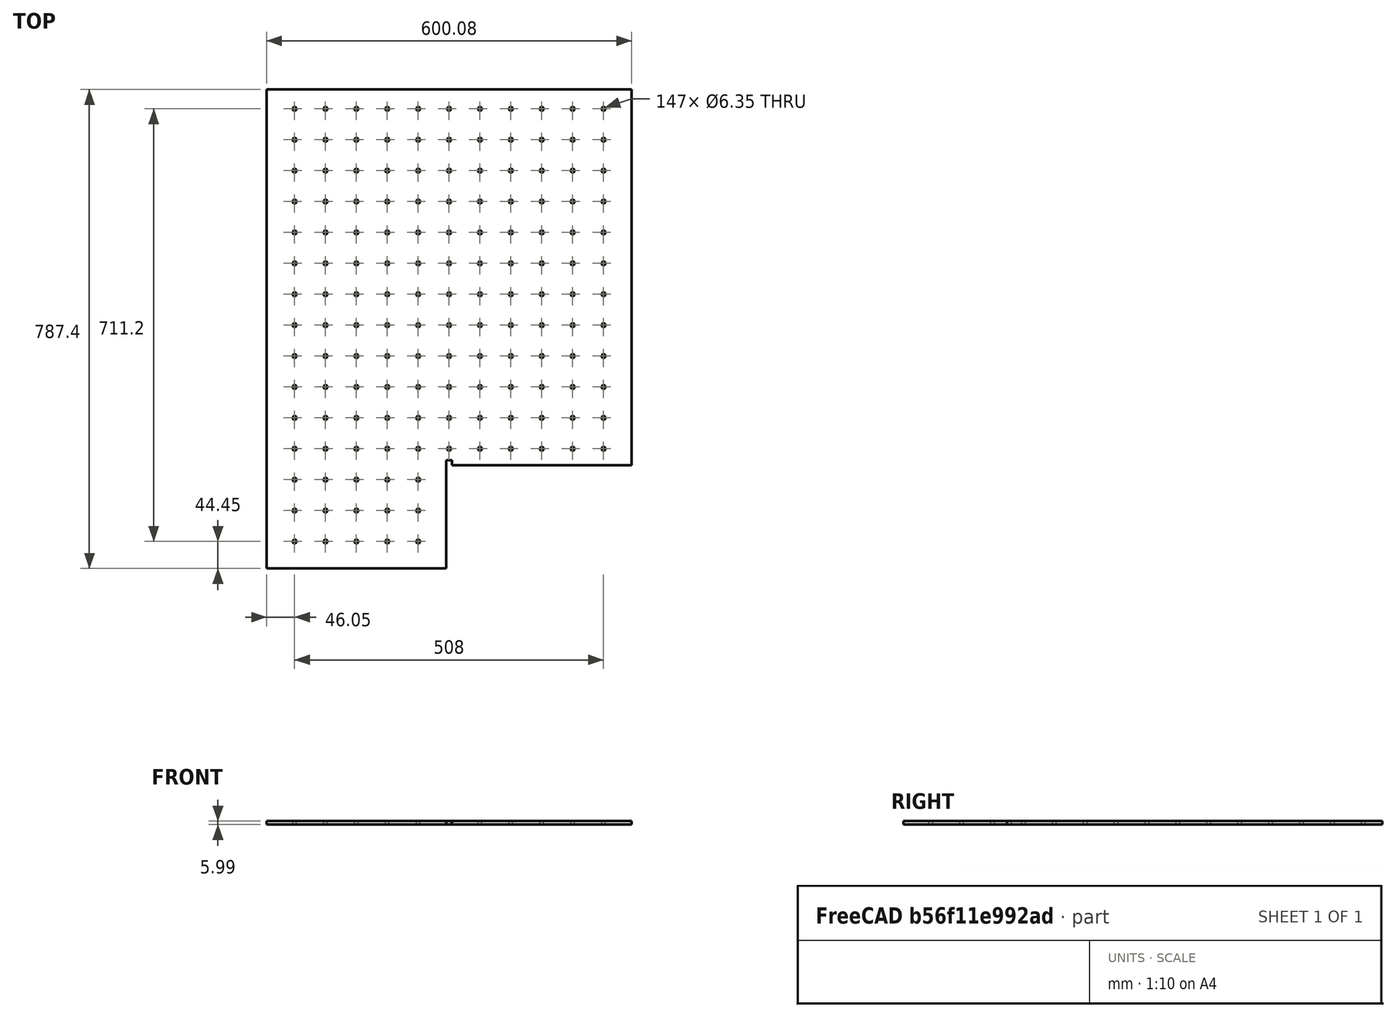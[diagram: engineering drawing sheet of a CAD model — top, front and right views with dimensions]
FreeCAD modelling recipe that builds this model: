
FCSTD DOCUMENT  (FreeCAD 0.19R24267 (Git))
Label: Inv2-P9
License: All rights reserved
LicenseURL: http://en.wikipedia.org/wiki/All_rights_reserved
objects: TechDraw::DrawViewDimension×13, TechDraw::DrawProjGroupItem×2, TechDraw::DrawHatch×2, TechDraw::DrawViewAnnotation×2, Sketcher::SketchObject×1, Part::Extrusion×1, TechDraw::DrawSVGTemplate×1, TechDraw::DrawProjGroup×1, TechDraw::DrawPage×1
note: 2 computed .brp shape members not serialized (recipe doc carries the construction recipe); baked Part::Feature solids carry a one-line shape summary decoded from their .brp

FEATURE [Sketcher::SketchObject] Sketch
  FullyConstrained = false
  sketch-geometry (301):
    g0: LineSegment StartX=0 StartY=0 StartZ=0 EndX=600.075 EndY=0 EndZ=0
    g1: LineSegment StartX=600.075 StartY=0 StartZ=0 EndX=600.075 EndY=-617.55 EndZ=0
    g2: LineSegment StartX=295.275 StartY=-609.6 StartZ=0 EndX=295.275 EndY=-787.4 EndZ=0
    g3: LineSegment StartX=295.275 StartY=-787.4 StartZ=0 EndX=0 EndY=-787.4 EndZ=0
    g4: LineSegment StartX=0 StartY=-787.4 StartZ=0 EndX=0 EndY=0 EndZ=0
    g5: Circle CenterX=46.0502 CenterY=-31.75 CenterZ=0 NormalX=0 NormalY=0 NormalZ=1 AngleXU=0 Radius=3.175
    g6: LineSegment StartX=295.275 StartY=-609.6 StartZ=0 EndX=304.8 EndY=-609.6 EndZ=0
    g7: LineSegment StartX=304.8 StartY=-609.6 StartZ=0 EndX=304.8 EndY=-617.55 EndZ=0
    g8: LineSegment StartX=304.8 StartY=-617.55 StartZ=0 EndX=600.075 EndY=-617.55 EndZ=0
    g9: Circle CenterX=96.8502 CenterY=-31.75 CenterZ=0 NormalX=0 NormalY=0 NormalZ=1 AngleXU=0 Radius=3.175
    g10: LineSegment StartX=46.0502 StartY=-31.75 StartZ=0 EndX=96.8502 EndY=-31.75 EndZ=0
    g11: Circle CenterX=147.65 CenterY=-31.75 CenterZ=0 NormalX=0 NormalY=0 NormalZ=1 AngleXU=0 Radius=3.175
    g12: LineSegment StartX=96.8502 StartY=-31.75 StartZ=0 EndX=147.65 EndY=-31.75 EndZ=0
    g13: Circle CenterX=198.45 CenterY=-31.75 CenterZ=0 NormalX=0 NormalY=0 NormalZ=1 AngleXU=0 Radius=3.175
    g14: LineSegment StartX=147.65 StartY=-31.75 StartZ=0 EndX=198.45 EndY=-31.75 EndZ=0
    g15: Circle CenterX=249.25 CenterY=-31.75 CenterZ=0 NormalX=0 NormalY=0 NormalZ=1 AngleXU=0 Radius=3.175
    g16: LineSegment StartX=198.45 StartY=-31.75 StartZ=0 EndX=249.25 EndY=-31.75 EndZ=0
    g17: Circle CenterX=300.05 CenterY=-31.75 CenterZ=0 NormalX=0 NormalY=0 NormalZ=1 AngleXU=0 Radius=3.175
    g18: LineSegment StartX=249.25 StartY=-31.75 StartZ=0 EndX=300.05 EndY=-31.75 EndZ=0
    g19: Circle CenterX=350.85 CenterY=-31.75 CenterZ=0 NormalX=0 NormalY=0 NormalZ=1 AngleXU=0 Radius=3.175
    g20: LineSegment StartX=300.05 StartY=-31.75 StartZ=0 EndX=350.85 EndY=-31.75 EndZ=0
    g21: Circle CenterX=401.65 CenterY=-31.75 CenterZ=0 NormalX=0 NormalY=0 NormalZ=1 AngleXU=0 Radius=3.175
    g22: LineSegment StartX=350.85 StartY=-31.75 StartZ=0 EndX=401.65 EndY=-31.75 EndZ=0
    g23: Circle CenterX=452.45 CenterY=-31.75 CenterZ=0 NormalX=0 NormalY=0 NormalZ=1 AngleXU=0 Radius=3.175
    g24: LineSegment StartX=401.65 StartY=-31.75 StartZ=0 EndX=452.45 EndY=-31.75 EndZ=0
    g25: Circle CenterX=503.25 CenterY=-31.75 CenterZ=0 NormalX=0 NormalY=0 NormalZ=1 AngleXU=0 Radius=3.175
    g26: LineSegment StartX=452.45 StartY=-31.75 StartZ=0 EndX=503.25 EndY=-31.75 EndZ=0
    g27: Circle CenterX=554.05 CenterY=-31.75 CenterZ=0 NormalX=0 NormalY=0 NormalZ=1 AngleXU=0 Radius=3.175
    g28: LineSegment StartX=503.25 StartY=-31.75 StartZ=0 EndX=554.05 EndY=-31.75 EndZ=0
    g29: Circle CenterX=46.0502 CenterY=-82.55 CenterZ=0 NormalX=0 NormalY=0 NormalZ=1 AngleXU=0 Radius=3.175
    g30: LineSegment StartX=46.0502 StartY=-31.75 StartZ=0 EndX=46.0502 EndY=-82.55 EndZ=0
    g31: Circle CenterX=96.8502 CenterY=-82.55 CenterZ=0 NormalX=0 NormalY=0 NormalZ=1 AngleXU=0 Radius=3.175
    g32: LineSegment StartX=46.0502 StartY=-82.55 StartZ=0 EndX=96.8502 EndY=-82.55 EndZ=0
    g33: Circle CenterX=147.65 CenterY=-82.55 CenterZ=0 NormalX=0 NormalY=0 NormalZ=1 AngleXU=0 Radius=3.175
    g34: LineSegment StartX=96.8502 StartY=-82.55 StartZ=0 EndX=147.65 EndY=-82.55 EndZ=0
    g35: Circle CenterX=198.45 CenterY=-82.55 CenterZ=0 NormalX=0 NormalY=0 NormalZ=1 AngleXU=0 Radius=3.175
    g36: LineSegment StartX=147.65 StartY=-82.55 StartZ=0 EndX=198.45 EndY=-82.55 EndZ=0
    g37: Circle CenterX=249.25 CenterY=-82.55 CenterZ=0 NormalX=0 NormalY=0 NormalZ=1 AngleXU=0 Radius=3.175
    g38: LineSegment StartX=198.45 StartY=-82.55 StartZ=0 EndX=249.25 EndY=-82.55 EndZ=0
    g39: Circle CenterX=300.05 CenterY=-82.55 CenterZ=0 NormalX=0 NormalY=0 NormalZ=1 AngleXU=0 Radius=3.175
    g40: LineSegment StartX=249.25 StartY=-82.55 StartZ=0 EndX=300.05 EndY=-82.55 EndZ=0
    g41: Circle CenterX=350.85 CenterY=-82.55 CenterZ=0 NormalX=0 NormalY=0 NormalZ=1 AngleXU=0 Radius=3.175
    g42: LineSegment StartX=300.05 StartY=-82.55 StartZ=0 EndX=350.85 EndY=-82.55 EndZ=0
    g43: Circle CenterX=401.65 CenterY=-82.55 CenterZ=0 NormalX=0 NormalY=0 NormalZ=1 AngleXU=0 Radius=3.175
    g44: LineSegment StartX=350.85 StartY=-82.55 StartZ=0 EndX=401.65 EndY=-82.55 EndZ=0
    g45: Circle CenterX=452.45 CenterY=-82.55 CenterZ=0 NormalX=0 NormalY=0 NormalZ=1 AngleXU=0 Radius=3.175
    g46: LineSegment StartX=401.65 StartY=-82.55 StartZ=0 EndX=452.45 EndY=-82.55 EndZ=0
    g47: Circle CenterX=503.25 CenterY=-82.55 CenterZ=0 NormalX=0 NormalY=0 NormalZ=1 AngleXU=0 Radius=3.175
    g48: LineSegment StartX=452.45 StartY=-82.55 StartZ=0 EndX=503.25 EndY=-82.55 EndZ=0
    g49: Circle CenterX=554.05 CenterY=-82.55 CenterZ=0 NormalX=0 NormalY=0 NormalZ=1 AngleXU=0 Radius=3.175
    g50: LineSegment StartX=503.25 StartY=-82.55 StartZ=0 EndX=554.05 EndY=-82.55 EndZ=0
    g51: Circle CenterX=46.0502 CenterY=-133.35 CenterZ=0 NormalX=0 NormalY=0 NormalZ=1 AngleXU=0 Radius=3.175
    g52: LineSegment StartX=46.0502 StartY=-82.55 StartZ=0 EndX=46.0502 EndY=-133.35 EndZ=0
    g53: Circle CenterX=96.8502 CenterY=-133.35 CenterZ=0 NormalX=0 NormalY=0 NormalZ=1 AngleXU=0 Radius=3.175
    g54: LineSegment StartX=46.0502 StartY=-133.35 StartZ=0 EndX=96.8502 EndY=-133.35 EndZ=0
    g55: Circle CenterX=147.65 CenterY=-133.35 CenterZ=0 NormalX=0 NormalY=0 NormalZ=1 AngleXU=0 Radius=3.175
    g56: LineSegment StartX=96.8502 StartY=-133.35 StartZ=0 EndX=147.65 EndY=-133.35 EndZ=0
    g57: Circle CenterX=198.45 CenterY=-133.35 CenterZ=0 NormalX=0 NormalY=0 NormalZ=1 AngleXU=0 Radius=3.175
    g58: LineSegment StartX=147.65 StartY=-133.35 StartZ=0 EndX=198.45 EndY=-133.35 EndZ=0
    g59: Circle CenterX=249.25 CenterY=-133.35 CenterZ=0 NormalX=0 NormalY=0 NormalZ=1 AngleXU=0 Radius=3.175
    g60: LineSegment StartX=198.45 StartY=-133.35 StartZ=0 EndX=249.25 EndY=-133.35 EndZ=0
    g61: Circle CenterX=300.05 CenterY=-133.35 CenterZ=0 NormalX=0 NormalY=0 NormalZ=1 AngleXU=0 Radius=3.175
    g62: LineSegment StartX=249.25 StartY=-133.35 StartZ=0 EndX=300.05 EndY=-133.35 EndZ=0
    g63: Circle CenterX=350.85 CenterY=-133.35 CenterZ=0 NormalX=0 NormalY=0 NormalZ=1 AngleXU=0 Radius=3.175
    g64: LineSegment StartX=300.05 StartY=-133.35 StartZ=0 EndX=350.85 EndY=-133.35 EndZ=0
    g65: Circle CenterX=401.65 CenterY=-133.35 CenterZ=0 NormalX=0 NormalY=0 NormalZ=1 AngleXU=0 Radius=3.175
    g66: LineSegment StartX=350.85 StartY=-133.35 StartZ=0 EndX=401.65 EndY=-133.35 EndZ=0
    g67: Circle CenterX=452.45 CenterY=-133.35 CenterZ=0 NormalX=0 NormalY=0 NormalZ=1 AngleXU=0 Radius=3.175
    g68: LineSegment StartX=401.65 StartY=-133.35 StartZ=0 EndX=452.45 EndY=-133.35 EndZ=0
    g69: Circle CenterX=503.25 CenterY=-133.35 CenterZ=0 NormalX=0 NormalY=0 NormalZ=1 AngleXU=0 Radius=3.175
    g70: LineSegment StartX=452.45 StartY=-133.35 StartZ=0 EndX=503.25 EndY=-133.35 EndZ=0
    g71: Circle CenterX=554.05 CenterY=-133.35 CenterZ=0 NormalX=0 NormalY=0 NormalZ=1 AngleXU=0 Radius=3.175
    g72: LineSegment StartX=503.25 StartY=-133.35 StartZ=0 EndX=554.05 EndY=-133.35 EndZ=0
    g73: Circle CenterX=46.0502 CenterY=-184.15 CenterZ=0 NormalX=0 NormalY=0 NormalZ=1 AngleXU=0 Radius=3.175
    g74: LineSegment StartX=46.0502 StartY=-133.35 StartZ=0 EndX=46.0502 EndY=-184.15 EndZ=0
    g75: Circle CenterX=96.8502 CenterY=-184.15 CenterZ=0 NormalX=0 NormalY=0 NormalZ=1 AngleXU=0 Radius=3.175
    g76: LineSegment StartX=46.0502 StartY=-184.15 StartZ=0 EndX=96.8502 EndY=-184.15 EndZ=0
    g77: Circle CenterX=147.65 CenterY=-184.15 CenterZ=0 NormalX=0 NormalY=0 NormalZ=1 AngleXU=0 Radius=3.175
    g78: LineSegment StartX=96.8502 StartY=-184.15 StartZ=0 EndX=147.65 EndY=-184.15 EndZ=0
    g79: Circle CenterX=198.45 CenterY=-184.15 CenterZ=0 NormalX=0 NormalY=0 NormalZ=1 AngleXU=0 Radius=3.175
    g80: LineSegment StartX=147.65 StartY=-184.15 StartZ=0 EndX=198.45 EndY=-184.15 EndZ=0
    g81: Circle CenterX=249.25 CenterY=-184.15 CenterZ=0 NormalX=0 NormalY=0 NormalZ=1 AngleXU=0 Radius=3.175
    g82: LineSegment StartX=198.45 StartY=-184.15 StartZ=0 EndX=249.25 EndY=-184.15 EndZ=0
    g83: Circle CenterX=300.05 CenterY=-184.15 CenterZ=0 NormalX=0 NormalY=0 NormalZ=1 AngleXU=0 Radius=3.175
    g84: LineSegment StartX=249.25 StartY=-184.15 StartZ=0 EndX=300.05 EndY=-184.15 EndZ=0
    g85: Circle CenterX=350.85 CenterY=-184.15 CenterZ=0 NormalX=0 NormalY=0 NormalZ=1 AngleXU=0 Radius=3.175
    g86: LineSegment StartX=300.05 StartY=-184.15 StartZ=0 EndX=350.85 EndY=-184.15 EndZ=0
    g87: Circle CenterX=401.65 CenterY=-184.15 CenterZ=0 NormalX=0 NormalY=0 NormalZ=1 AngleXU=0 Radius=3.175
    g88: LineSegment StartX=350.85 StartY=-184.15 StartZ=0 EndX=401.65 EndY=-184.15 EndZ=0
    g89: Circle CenterX=452.45 CenterY=-184.15 CenterZ=0 NormalX=0 NormalY=0 NormalZ=1 AngleXU=0 Radius=3.175
    g90: LineSegment StartX=401.65 StartY=-184.15 StartZ=0 EndX=452.45 EndY=-184.15 EndZ=0
    g91: Circle CenterX=503.25 CenterY=-184.15 CenterZ=0 NormalX=0 NormalY=0 NormalZ=1 AngleXU=0 Radius=3.175
    g92: LineSegment StartX=452.45 StartY=-184.15 StartZ=0 EndX=503.25 EndY=-184.15 EndZ=0
    g93: Circle CenterX=554.05 CenterY=-184.15 CenterZ=0 NormalX=0 NormalY=0 NormalZ=1 AngleXU=0 Radius=3.175
    g94: LineSegment StartX=503.25 StartY=-184.15 StartZ=0 EndX=554.05 EndY=-184.15 EndZ=0
    g95: Circle CenterX=46.0502 CenterY=-234.95 CenterZ=0 NormalX=0 NormalY=0 NormalZ=1 AngleXU=0 Radius=3.175
    g96: LineSegment StartX=46.0502 StartY=-184.15 StartZ=0 EndX=46.0502 EndY=-234.95 EndZ=0
    g97: Circle CenterX=96.8502 CenterY=-234.95 CenterZ=0 NormalX=0 NormalY=0 NormalZ=1 AngleXU=0 Radius=3.175
    g98: LineSegment StartX=46.0502 StartY=-234.95 StartZ=0 EndX=96.8502 EndY=-234.95 EndZ=0
    g99: Circle CenterX=147.65 CenterY=-234.95 CenterZ=0 NormalX=0 NormalY=0 NormalZ=1 AngleXU=0 Radius=3.175
    g100: LineSegment StartX=96.8502 StartY=-234.95 StartZ=0 EndX=147.65 EndY=-234.95 EndZ=0
    g101: Circle CenterX=198.45 CenterY=-234.95 CenterZ=0 NormalX=0 NormalY=0 NormalZ=1 AngleXU=0 Radius=3.175
    g102: LineSegment StartX=147.65 StartY=-234.95 StartZ=0 EndX=198.45 EndY=-234.95 EndZ=0
    g103: Circle CenterX=249.25 CenterY=-234.95 CenterZ=0 NormalX=0 NormalY=0 NormalZ=1 AngleXU=0 Radius=3.175
    g104: LineSegment StartX=198.45 StartY=-234.95 StartZ=0 EndX=249.25 EndY=-234.95 EndZ=0
    g105: Circle CenterX=300.05 CenterY=-234.95 CenterZ=0 NormalX=0 NormalY=0 NormalZ=1 AngleXU=0 Radius=3.175
    g106: LineSegment StartX=249.25 StartY=-234.95 StartZ=0 EndX=300.05 EndY=-234.95 EndZ=0
    g107: Circle CenterX=350.85 CenterY=-234.95 CenterZ=0 NormalX=0 NormalY=0 NormalZ=1 AngleXU=0 Radius=3.175
    g108: LineSegment StartX=300.05 StartY=-234.95 StartZ=0 EndX=350.85 EndY=-234.95 EndZ=0
    g109: Circle CenterX=401.65 CenterY=-234.95 CenterZ=0 NormalX=0 NormalY=0 NormalZ=1 AngleXU=0 Radius=3.175
    g110: LineSegment StartX=350.85 StartY=-234.95 StartZ=0 EndX=401.65 EndY=-234.95 EndZ=0
    g111: Circle CenterX=452.45 CenterY=-234.95 CenterZ=0 NormalX=0 NormalY=0 NormalZ=1 AngleXU=0 Radius=3.175
    g112: LineSegment StartX=401.65 StartY=-234.95 StartZ=0 EndX=452.45 EndY=-234.95 EndZ=0
    g113: Circle CenterX=503.25 CenterY=-234.95 CenterZ=0 NormalX=0 NormalY=0 NormalZ=1 AngleXU=0 Radius=3.175
    g114: LineSegment StartX=452.45 StartY=-234.95 StartZ=0 EndX=503.25 EndY=-234.95 EndZ=0
    g115: Circle CenterX=554.05 CenterY=-234.95 CenterZ=0 NormalX=0 NormalY=0 NormalZ=1 AngleXU=0 Radius=3.175
    g116: LineSegment StartX=503.25 StartY=-234.95 StartZ=0 EndX=554.05 EndY=-234.95 EndZ=0
    g117: Circle CenterX=46.0502 CenterY=-285.75 CenterZ=0 NormalX=0 NormalY=0 NormalZ=1 AngleXU=0 Radius=3.175
    g118: LineSegment StartX=46.0502 StartY=-234.95 StartZ=0 EndX=46.0502 EndY=-285.75 EndZ=0
    g119: Circle CenterX=96.8502 CenterY=-285.75 CenterZ=0 NormalX=0 NormalY=0 NormalZ=1 AngleXU=0 Radius=3.175
    g120: LineSegment StartX=46.0502 StartY=-285.75 StartZ=0 EndX=96.8502 EndY=-285.75 EndZ=0
    g121: Circle CenterX=147.65 CenterY=-285.75 CenterZ=0 NormalX=0 NormalY=0 NormalZ=1 AngleXU=0 Radius=3.175
    g122: LineSegment StartX=96.8502 StartY=-285.75 StartZ=0 EndX=147.65 EndY=-285.75 EndZ=0
    g123: Circle CenterX=198.45 CenterY=-285.75 CenterZ=0 NormalX=0 NormalY=0 NormalZ=1 AngleXU=0 Radius=3.175
    g124: LineSegment StartX=147.65 StartY=-285.75 StartZ=0 EndX=198.45 EndY=-285.75 EndZ=0
    g125: Circle CenterX=249.25 CenterY=-285.75 CenterZ=0 NormalX=0 NormalY=0 NormalZ=1 AngleXU=0 Radius=3.175
    g126: LineSegment StartX=198.45 StartY=-285.75 StartZ=0 EndX=249.25 EndY=-285.75 EndZ=0
    g127: Circle CenterX=300.05 CenterY=-285.75 CenterZ=0 NormalX=0 NormalY=0 NormalZ=1 AngleXU=0 Radius=3.175
    g128: LineSegment StartX=249.25 StartY=-285.75 StartZ=0 EndX=300.05 EndY=-285.75 EndZ=0
    g129: Circle CenterX=350.85 CenterY=-285.75 CenterZ=0 NormalX=0 NormalY=0 NormalZ=1 AngleXU=0 Radius=3.175
    g130: LineSegment StartX=300.05 StartY=-285.75 StartZ=0 EndX=350.85 EndY=-285.75 EndZ=0
    g131: Circle CenterX=401.65 CenterY=-285.75 CenterZ=0 NormalX=0 NormalY=0 NormalZ=1 AngleXU=0 Radius=3.175
    g132: LineSegment StartX=350.85 StartY=-285.75 StartZ=0 EndX=401.65 EndY=-285.75 EndZ=0
    g133: Circle CenterX=452.45 CenterY=-285.75 CenterZ=0 NormalX=0 NormalY=0 NormalZ=1 AngleXU=0 Radius=3.175
    g134: LineSegment StartX=401.65 StartY=-285.75 StartZ=0 EndX=452.45 EndY=-285.75 EndZ=0
    g135: Circle CenterX=503.25 CenterY=-285.75 CenterZ=0 NormalX=0 NormalY=0 NormalZ=1 AngleXU=0 Radius=3.175
    g136: LineSegment StartX=452.45 StartY=-285.75 StartZ=0 EndX=503.25 EndY=-285.75 EndZ=0
    g137: Circle CenterX=554.05 CenterY=-285.75 CenterZ=0 NormalX=0 NormalY=0 NormalZ=1 AngleXU=0 Radius=3.175
    g138: LineSegment StartX=503.25 StartY=-285.75 StartZ=0 EndX=554.05 EndY=-285.75 EndZ=0
    g139: Circle CenterX=46.0502 CenterY=-336.55 CenterZ=0 NormalX=0 NormalY=0 NormalZ=1 AngleXU=0 Radius=3.175
    g140: LineSegment StartX=46.0502 StartY=-285.75 StartZ=0 EndX=46.0502 EndY=-336.55 EndZ=0
    g141: Circle CenterX=96.8502 CenterY=-336.55 CenterZ=0 NormalX=0 NormalY=0 NormalZ=1 AngleXU=0 Radius=3.175
    g142: LineSegment StartX=46.0502 StartY=-336.55 StartZ=0 EndX=96.8502 EndY=-336.55 EndZ=0
    g143: Circle CenterX=147.65 CenterY=-336.55 CenterZ=0 NormalX=0 NormalY=0 NormalZ=1 AngleXU=0 Radius=3.175
    g144: LineSegment StartX=96.8502 StartY=-336.55 StartZ=0 EndX=147.65 EndY=-336.55 EndZ=0
    g145: Circle CenterX=198.45 CenterY=-336.55 CenterZ=0 NormalX=0 NormalY=0 NormalZ=1 AngleXU=0 Radius=3.175
    g146: LineSegment StartX=147.65 StartY=-336.55 StartZ=0 EndX=198.45 EndY=-336.55 EndZ=0
    g147: Circle CenterX=249.25 CenterY=-336.55 CenterZ=0 NormalX=0 NormalY=0 NormalZ=1 AngleXU=0 Radius=3.175
    g148: LineSegment StartX=198.45 StartY=-336.55 StartZ=0 EndX=249.25 EndY=-336.55 EndZ=0
    g149: Circle CenterX=300.05 CenterY=-336.55 CenterZ=0 NormalX=0 NormalY=0 NormalZ=1 AngleXU=0 Radius=3.175
    g150: LineSegment StartX=249.25 StartY=-336.55 StartZ=0 EndX=300.05 EndY=-336.55 EndZ=0
    g151: Circle CenterX=350.85 CenterY=-336.55 CenterZ=0 NormalX=0 NormalY=0 NormalZ=1 AngleXU=0 Radius=3.175
    g152: LineSegment StartX=300.05 StartY=-336.55 StartZ=0 EndX=350.85 EndY=-336.55 EndZ=0
    g153: Circle CenterX=401.65 CenterY=-336.55 CenterZ=0 NormalX=0 NormalY=0 NormalZ=1 AngleXU=0 Radius=3.175
    g154: LineSegment StartX=350.85 StartY=-336.55 StartZ=0 EndX=401.65 EndY=-336.55 EndZ=0
    g155: Circle CenterX=452.45 CenterY=-336.55 CenterZ=0 NormalX=0 NormalY=0 NormalZ=1 AngleXU=0 Radius=3.175
    g156: LineSegment StartX=401.65 StartY=-336.55 StartZ=0 EndX=452.45 EndY=-336.55 EndZ=0
    g157: Circle CenterX=503.25 CenterY=-336.55 CenterZ=0 NormalX=0 NormalY=0 NormalZ=1 AngleXU=0 Radius=3.175
    g158: LineSegment StartX=452.45 StartY=-336.55 StartZ=0 EndX=503.25 EndY=-336.55 EndZ=0
    g159: Circle CenterX=554.05 CenterY=-336.55 CenterZ=0 NormalX=0 NormalY=0 NormalZ=1 AngleXU=0 Radius=3.175
    g160: LineSegment StartX=503.25 StartY=-336.55 StartZ=0 EndX=554.05 EndY=-336.55 EndZ=0
    g161: Circle CenterX=46.0502 CenterY=-387.35 CenterZ=0 NormalX=0 NormalY=0 NormalZ=1 AngleXU=0 Radius=3.175
    g162: LineSegment StartX=46.0502 StartY=-336.55 StartZ=0 EndX=46.0502 EndY=-387.35 EndZ=0
    g163: Circle CenterX=96.8502 CenterY=-387.35 CenterZ=0 NormalX=0 NormalY=0 NormalZ=1 AngleXU=0 Radius=3.175
    g164: LineSegment StartX=46.0502 StartY=-387.35 StartZ=0 EndX=96.8502 EndY=-387.35 EndZ=0
    g165: Circle CenterX=147.65 CenterY=-387.35 CenterZ=0 NormalX=0 NormalY=0 NormalZ=1 AngleXU=0 Radius=3.175
    g166: LineSegment StartX=96.8502 StartY=-387.35 StartZ=0 EndX=147.65 EndY=-387.35 EndZ=0
    g167: Circle CenterX=198.45 CenterY=-387.35 CenterZ=0 NormalX=0 NormalY=0 NormalZ=1 AngleXU=0 Radius=3.175
    g168: LineSegment StartX=147.65 StartY=-387.35 StartZ=0 EndX=198.45 EndY=-387.35 EndZ=0
    g169: Circle CenterX=249.25 CenterY=-387.35 CenterZ=0 NormalX=0 NormalY=0 NormalZ=1 AngleXU=0 Radius=3.175
    g170: LineSegment StartX=198.45 StartY=-387.35 StartZ=0 EndX=249.25 EndY=-387.35 EndZ=0
    g171: Circle CenterX=300.05 CenterY=-387.35 CenterZ=0 NormalX=0 NormalY=0 NormalZ=1 AngleXU=0 Radius=3.175
    g172: LineSegment StartX=249.25 StartY=-387.35 StartZ=0 EndX=300.05 EndY=-387.35 EndZ=0
    g173: Circle CenterX=350.85 CenterY=-387.35 CenterZ=0 NormalX=0 NormalY=0 NormalZ=1 AngleXU=0 Radius=3.175
    g174: LineSegment StartX=300.05 StartY=-387.35 StartZ=0 EndX=350.85 EndY=-387.35 EndZ=0
    g175: Circle CenterX=401.65 CenterY=-387.35 CenterZ=0 NormalX=0 NormalY=0 NormalZ=1 AngleXU=0 Radius=3.175
    g176: LineSegment StartX=350.85 StartY=-387.35 StartZ=0 EndX=401.65 EndY=-387.35 EndZ=0
    g177: Circle CenterX=452.45 CenterY=-387.35 CenterZ=0 NormalX=0 NormalY=0 NormalZ=1 AngleXU=0 Radius=3.175
    g178: LineSegment StartX=401.65 StartY=-387.35 StartZ=0 EndX=452.45 EndY=-387.35 EndZ=0
    g179: Circle CenterX=503.25 CenterY=-387.35 CenterZ=0 NormalX=0 NormalY=0 NormalZ=1 AngleXU=0 Radius=3.175
    g180: LineSegment StartX=452.45 StartY=-387.35 StartZ=0 EndX=503.25 EndY=-387.35 EndZ=0
    g181: Circle CenterX=554.05 CenterY=-387.35 CenterZ=0 NormalX=0 NormalY=0 NormalZ=1 AngleXU=0 Radius=3.175
    g182: LineSegment StartX=503.25 StartY=-387.35 StartZ=0 EndX=554.05 EndY=-387.35 EndZ=0
    g183: Circle CenterX=46.0502 CenterY=-438.15 CenterZ=0 NormalX=0 NormalY=0 NormalZ=1 AngleXU=0 Radius=3.175
    g184: LineSegment StartX=46.0502 StartY=-387.35 StartZ=0 EndX=46.0502 EndY=-438.15 EndZ=0
    g185: Circle CenterX=96.8502 CenterY=-438.15 CenterZ=0 NormalX=0 NormalY=0 NormalZ=1 AngleXU=0 Radius=3.175
    g186: LineSegment StartX=46.0502 StartY=-438.15 StartZ=0 EndX=96.8502 EndY=-438.15 EndZ=0
    g187: Circle CenterX=147.65 CenterY=-438.15 CenterZ=0 NormalX=0 NormalY=0 NormalZ=1 AngleXU=0 Radius=3.175
    g188: LineSegment StartX=96.8502 StartY=-438.15 StartZ=0 EndX=147.65 EndY=-438.15 EndZ=0
    g189: Circle CenterX=198.45 CenterY=-438.15 CenterZ=0 NormalX=0 NormalY=0 NormalZ=1 AngleXU=0 Radius=3.175
    g190: LineSegment StartX=147.65 StartY=-438.15 StartZ=0 EndX=198.45 EndY=-438.15 EndZ=0
    g191: Circle CenterX=249.25 CenterY=-438.15 CenterZ=0 NormalX=0 NormalY=0 NormalZ=1 AngleXU=0 Radius=3.175
    g192: LineSegment StartX=198.45 StartY=-438.15 StartZ=0 EndX=249.25 EndY=-438.15 EndZ=0
    g193: Circle CenterX=300.05 CenterY=-438.15 CenterZ=0 NormalX=0 NormalY=0 NormalZ=1 AngleXU=0 Radius=3.175
    g194: LineSegment StartX=249.25 StartY=-438.15 StartZ=0 EndX=300.05 EndY=-438.15 EndZ=0
    g195: Circle CenterX=350.85 CenterY=-438.15 CenterZ=0 NormalX=0 NormalY=0 NormalZ=1 AngleXU=0 Radius=3.175
    g196: LineSegment StartX=300.05 StartY=-438.15 StartZ=0 EndX=350.85 EndY=-438.15 EndZ=0
    g197: Circle CenterX=401.65 CenterY=-438.15 CenterZ=0 NormalX=0 NormalY=0 NormalZ=1 AngleXU=0 Radius=3.175
    g198: LineSegment StartX=350.85 StartY=-438.15 StartZ=0 EndX=401.65 EndY=-438.15 EndZ=0
    g199: Circle CenterX=452.45 CenterY=-438.15 CenterZ=0 NormalX=0 NormalY=0 NormalZ=1 AngleXU=0 Radius=3.175
    g200: LineSegment StartX=401.65 StartY=-438.15 StartZ=0 EndX=452.45 EndY=-438.15 EndZ=0
    g201: Circle CenterX=503.25 CenterY=-438.15 CenterZ=0 NormalX=0 NormalY=0 NormalZ=1 AngleXU=0 Radius=3.175
    g202: LineSegment StartX=452.45 StartY=-438.15 StartZ=0 EndX=503.25 EndY=-438.15 EndZ=0
    g203: Circle CenterX=554.05 CenterY=-438.15 CenterZ=0 NormalX=0 NormalY=0 NormalZ=1 AngleXU=0 Radius=3.175
    g204: LineSegment StartX=503.25 StartY=-438.15 StartZ=0 EndX=554.05 EndY=-438.15 EndZ=0
    g205: Circle CenterX=46.0502 CenterY=-488.95 CenterZ=0 NormalX=0 NormalY=0 NormalZ=1 AngleXU=0 Radius=3.175
    g206: LineSegment StartX=46.0502 StartY=-438.15 StartZ=0 EndX=46.0502 EndY=-488.95 EndZ=0
    g207: Circle CenterX=96.8502 CenterY=-488.95 CenterZ=0 NormalX=0 NormalY=0 NormalZ=1 AngleXU=0 Radius=3.175
    g208: LineSegment StartX=46.0502 StartY=-488.95 StartZ=0 EndX=96.8502 EndY=-488.95 EndZ=0
    g209: Circle CenterX=147.65 CenterY=-488.95 CenterZ=0 NormalX=0 NormalY=0 NormalZ=1 AngleXU=0 Radius=3.175
    g210: LineSegment StartX=96.8502 StartY=-488.95 StartZ=0 EndX=147.65 EndY=-488.95 EndZ=0
    g211: Circle CenterX=198.45 CenterY=-488.95 CenterZ=0 NormalX=0 NormalY=0 NormalZ=1 AngleXU=0 Radius=3.175
    g212: LineSegment StartX=147.65 StartY=-488.95 StartZ=0 EndX=198.45 EndY=-488.95 EndZ=0
    g213: Circle CenterX=249.25 CenterY=-488.95 CenterZ=0 NormalX=0 NormalY=0 NormalZ=1 AngleXU=0 Radius=3.175
    g214: LineSegment StartX=198.45 StartY=-488.95 StartZ=0 EndX=249.25 EndY=-488.95 EndZ=0
    g215: Circle CenterX=300.05 CenterY=-488.95 CenterZ=0 NormalX=0 NormalY=0 NormalZ=1 AngleXU=0 Radius=3.175
    g216: LineSegment StartX=249.25 StartY=-488.95 StartZ=0 EndX=300.05 EndY=-488.95 EndZ=0
    g217: Circle CenterX=350.85 CenterY=-488.95 CenterZ=0 NormalX=0 NormalY=0 NormalZ=1 AngleXU=0 Radius=3.175
    g218: LineSegment StartX=300.05 StartY=-488.95 StartZ=0 EndX=350.85 EndY=-488.95 EndZ=0
    g219: Circle CenterX=401.65 CenterY=-488.95 CenterZ=0 NormalX=0 NormalY=0 NormalZ=1 AngleXU=0 Radius=3.175
    g220: LineSegment StartX=350.85 StartY=-488.95 StartZ=0 EndX=401.65 EndY=-488.95 EndZ=0
    g221: Circle CenterX=452.45 CenterY=-488.95 CenterZ=0 NormalX=0 NormalY=0 NormalZ=1 AngleXU=0 Radius=3.175
    g222: LineSegment StartX=401.65 StartY=-488.95 StartZ=0 EndX=452.45 EndY=-488.95 EndZ=0
    g223: Circle CenterX=503.25 CenterY=-488.95 CenterZ=0 NormalX=0 NormalY=0 NormalZ=1 AngleXU=0 Radius=3.175
    g224: LineSegment StartX=452.45 StartY=-488.95 StartZ=0 EndX=503.25 EndY=-488.95 EndZ=0
    g225: Circle CenterX=554.05 CenterY=-488.95 CenterZ=0 NormalX=0 NormalY=0 NormalZ=1 AngleXU=0 Radius=3.175
    g226: LineSegment StartX=503.25 StartY=-488.95 StartZ=0 EndX=554.05 EndY=-488.95 EndZ=0
    g227: Circle CenterX=46.0502 CenterY=-539.75 CenterZ=0 NormalX=0 NormalY=0 NormalZ=1 AngleXU=0 Radius=3.175
    g228: LineSegment StartX=46.0502 StartY=-488.95 StartZ=0 EndX=46.0502 EndY=-539.75 EndZ=0
    g229: Circle CenterX=96.8502 CenterY=-539.75 CenterZ=0 NormalX=0 NormalY=0 NormalZ=1 AngleXU=0 Radius=3.175
    g230: LineSegment StartX=46.0502 StartY=-539.75 StartZ=0 EndX=96.8502 EndY=-539.75 EndZ=0
    g231: Circle CenterX=147.65 CenterY=-539.75 CenterZ=0 NormalX=0 NormalY=0 NormalZ=1 AngleXU=0 Radius=3.175
    g232: LineSegment StartX=96.8502 StartY=-539.75 StartZ=0 EndX=147.65 EndY=-539.75 EndZ=0
    g233: Circle CenterX=198.45 CenterY=-539.75 CenterZ=0 NormalX=0 NormalY=0 NormalZ=1 AngleXU=0 Radius=3.175
    g234: LineSegment StartX=147.65 StartY=-539.75 StartZ=0 EndX=198.45 EndY=-539.75 EndZ=0
    g235: Circle CenterX=249.25 CenterY=-539.75 CenterZ=0 NormalX=0 NormalY=0 NormalZ=1 AngleXU=0 Radius=3.175
    g236: LineSegment StartX=198.45 StartY=-539.75 StartZ=0 EndX=249.25 EndY=-539.75 EndZ=0
    g237: Circle CenterX=300.05 CenterY=-539.75 CenterZ=0 NormalX=0 NormalY=0 NormalZ=1 AngleXU=0 Radius=3.175
    g238: LineSegment StartX=249.25 StartY=-539.75 StartZ=0 EndX=300.05 EndY=-539.75 EndZ=0
    g239: Circle CenterX=350.85 CenterY=-539.75 CenterZ=0 NormalX=0 NormalY=0 NormalZ=1 AngleXU=0 Radius=3.175
    g240: LineSegment StartX=300.05 StartY=-539.75 StartZ=0 EndX=350.85 EndY=-539.75 EndZ=0
    g241: Circle CenterX=401.65 CenterY=-539.75 CenterZ=0 NormalX=0 NormalY=0 NormalZ=1 AngleXU=0 Radius=3.175
    g242: LineSegment StartX=350.85 StartY=-539.75 StartZ=0 EndX=401.65 EndY=-539.75 EndZ=0
    g243: Circle CenterX=452.45 CenterY=-539.75 CenterZ=0 NormalX=0 NormalY=0 NormalZ=1 AngleXU=0 Radius=3.175
    g244: LineSegment StartX=401.65 StartY=-539.75 StartZ=0 EndX=452.45 EndY=-539.75 EndZ=0
    g245: Circle CenterX=503.25 CenterY=-539.75 CenterZ=0 NormalX=0 NormalY=0 NormalZ=1 AngleXU=0 Radius=3.175
    g246: LineSegment StartX=452.45 StartY=-539.75 StartZ=0 EndX=503.25 EndY=-539.75 EndZ=0
    g247: Circle CenterX=554.05 CenterY=-539.75 CenterZ=0 NormalX=0 NormalY=0 NormalZ=1 AngleXU=0 Radius=3.175
    g248: LineSegment StartX=503.25 StartY=-539.75 StartZ=0 EndX=554.05 EndY=-539.75 EndZ=0
    g249: Circle CenterX=46.0502 CenterY=-590.55 CenterZ=0 NormalX=0 NormalY=0 NormalZ=1 AngleXU=0 Radius=3.175
    g250: LineSegment StartX=46.0502 StartY=-539.75 StartZ=0 EndX=46.0502 EndY=-590.55 EndZ=0
    g251: Circle CenterX=96.8502 CenterY=-590.55 CenterZ=0 NormalX=0 NormalY=0 NormalZ=1 AngleXU=0 Radius=3.175
    g252: LineSegment StartX=46.0502 StartY=-590.55 StartZ=0 EndX=96.8502 EndY=-590.55 EndZ=0
    g253: Circle CenterX=147.65 CenterY=-590.55 CenterZ=0 NormalX=0 NormalY=0 NormalZ=1 AngleXU=0 Radius=3.175
    g254: LineSegment StartX=96.8502 StartY=-590.55 StartZ=0 EndX=147.65 EndY=-590.55 EndZ=0
    g255: Circle CenterX=198.45 CenterY=-590.55 CenterZ=0 NormalX=0 NormalY=0 NormalZ=1 AngleXU=0 Radius=3.175
    g256: LineSegment StartX=147.65 StartY=-590.55 StartZ=0 EndX=198.45 EndY=-590.55 EndZ=0
    g257: Circle CenterX=249.25 CenterY=-590.55 CenterZ=0 NormalX=0 NormalY=0 NormalZ=1 AngleXU=0 Radius=3.175
    g258: LineSegment StartX=198.45 StartY=-590.55 StartZ=0 EndX=249.25 EndY=-590.55 EndZ=0
    g259: Circle CenterX=300.05 CenterY=-590.55 CenterZ=0 NormalX=0 NormalY=0 NormalZ=1 AngleXU=0 Radius=3.175
    g260: LineSegment StartX=249.25 StartY=-590.55 StartZ=0 EndX=300.05 EndY=-590.55 EndZ=0
    g261: Circle CenterX=350.85 CenterY=-590.55 CenterZ=0 NormalX=0 NormalY=0 NormalZ=1 AngleXU=0 Radius=3.175
    g262: LineSegment StartX=300.05 StartY=-590.55 StartZ=0 EndX=350.85 EndY=-590.55 EndZ=0
    g263: Circle CenterX=401.65 CenterY=-590.55 CenterZ=0 NormalX=0 NormalY=0 NormalZ=1 AngleXU=0 Radius=3.175
    g264: LineSegment StartX=350.85 StartY=-590.55 StartZ=0 EndX=401.65 EndY=-590.55 EndZ=0
    g265: Circle CenterX=452.45 CenterY=-590.55 CenterZ=0 NormalX=0 NormalY=0 NormalZ=1 AngleXU=0 Radius=3.175
    g266: LineSegment StartX=401.65 StartY=-590.55 StartZ=0 EndX=452.45 EndY=-590.55 EndZ=0
    g267: Circle CenterX=503.25 CenterY=-590.55 CenterZ=0 NormalX=0 NormalY=0 NormalZ=1 AngleXU=0 Radius=3.175
    g268: LineSegment StartX=452.45 StartY=-590.55 StartZ=0 EndX=503.25 EndY=-590.55 EndZ=0
    g269: Circle CenterX=554.05 CenterY=-590.55 CenterZ=0 NormalX=0 NormalY=0 NormalZ=1 AngleXU=0 Radius=3.175
    g270: LineSegment StartX=503.25 StartY=-590.55 StartZ=0 EndX=554.05 EndY=-590.55 EndZ=0
    g271: Circle CenterX=46.0502 CenterY=-641.35 CenterZ=0 NormalX=0 NormalY=0 NormalZ=1 AngleXU=0 Radius=3.175
    g272: LineSegment StartX=46.0502 StartY=-590.55 StartZ=0 EndX=46.0502 EndY=-641.35 EndZ=0
    g273: Circle CenterX=96.8502 CenterY=-641.35 CenterZ=0 NormalX=0 NormalY=0 NormalZ=1 AngleXU=0 Radius=3.175
    g274: LineSegment StartX=46.0502 StartY=-641.35 StartZ=0 EndX=96.8502 EndY=-641.35 EndZ=0
    g275: Circle CenterX=147.65 CenterY=-641.35 CenterZ=0 NormalX=0 NormalY=0 NormalZ=1 AngleXU=0 Radius=3.175
    g276: LineSegment StartX=96.8502 StartY=-641.35 StartZ=0 EndX=147.65 EndY=-641.35 EndZ=0
    g277: Circle CenterX=198.45 CenterY=-641.35 CenterZ=0 NormalX=0 NormalY=0 NormalZ=1 AngleXU=0 Radius=3.175
    g278: LineSegment StartX=147.65 StartY=-641.35 StartZ=0 EndX=198.45 EndY=-641.35 EndZ=0
    g279: Circle CenterX=249.25 CenterY=-641.35 CenterZ=0 NormalX=0 NormalY=0 NormalZ=1 AngleXU=0 Radius=3.175
    g280: LineSegment StartX=198.45 StartY=-641.35 StartZ=0 EndX=249.25 EndY=-641.35 EndZ=0
    g281: Circle CenterX=46.0502 CenterY=-692.15 CenterZ=0 NormalX=0 NormalY=0 NormalZ=1 AngleXU=0 Radius=3.175
    g282: LineSegment StartX=46.0502 StartY=-641.35 StartZ=0 EndX=46.0502 EndY=-692.15 EndZ=0
    g283: Circle CenterX=96.8502 CenterY=-692.15 CenterZ=0 NormalX=0 NormalY=0 NormalZ=1 AngleXU=0 Radius=3.175
    g284: LineSegment StartX=46.0502 StartY=-692.15 StartZ=0 EndX=96.8502 EndY=-692.15 EndZ=0
    g285: Circle CenterX=147.65 CenterY=-692.15 CenterZ=0 NormalX=0 NormalY=0 NormalZ=1 AngleXU=0 Radius=3.175
    g286: LineSegment StartX=96.8502 StartY=-692.15 StartZ=0 EndX=147.65 EndY=-692.15 EndZ=0
    g287: Circle CenterX=198.45 CenterY=-692.15 CenterZ=0 NormalX=0 NormalY=0 NormalZ=1 AngleXU=0 Radius=3.175
    g288: LineSegment StartX=147.65 StartY=-692.15 StartZ=0 EndX=198.45 EndY=-692.15 EndZ=0
    g289: Circle CenterX=249.25 CenterY=-692.15 CenterZ=0 NormalX=0 NormalY=0 NormalZ=1 AngleXU=0 Radius=3.175
    g290: LineSegment StartX=198.45 StartY=-692.15 StartZ=0 EndX=249.25 EndY=-692.15 EndZ=0
    g291: Circle CenterX=46.0502 CenterY=-742.95 CenterZ=0 NormalX=0 NormalY=0 NormalZ=1 AngleXU=0 Radius=3.175
    g292: LineSegment StartX=46.0502 StartY=-692.15 StartZ=0 EndX=46.0502 EndY=-742.95 EndZ=0
    g293: Circle CenterX=96.8502 CenterY=-742.95 CenterZ=0 NormalX=0 NormalY=0 NormalZ=1 AngleXU=0 Radius=3.175
    g294: LineSegment StartX=46.0502 StartY=-742.95 StartZ=0 EndX=96.8502 EndY=-742.95 EndZ=0
    g295: Circle CenterX=147.65 CenterY=-742.95 CenterZ=0 NormalX=0 NormalY=0 NormalZ=1 AngleXU=0 Radius=3.175
    g296: LineSegment StartX=96.8502 StartY=-742.95 StartZ=0 EndX=147.65 EndY=-742.95 EndZ=0
    g297: Circle CenterX=198.45 CenterY=-742.95 CenterZ=0 NormalX=0 NormalY=0 NormalZ=1 AngleXU=0 Radius=3.175
    g298: LineSegment StartX=147.65 StartY=-742.95 StartZ=0 EndX=198.45 EndY=-742.95 EndZ=0
    g299: Circle CenterX=249.25 CenterY=-742.95 CenterZ=0 NormalX=0 NormalY=0 NormalZ=1 AngleXU=0 Radius=3.175
    g300: LineSegment StartX=198.45 StartY=-742.95 StartZ=0 EndX=249.25 EndY=-742.95 EndZ=0
  constraints (755):
    c: Coincident(g0,g-1)
    c: PointOnObject(g0,g-1)
    c: Coincident(g1,g0)
    c: Vertical(g1)
    c: Coincident(g3,g2)
    c: PointOnObject(g3,g-2)
    c: Horizontal(g3)
    c: Coincident(g4,g3)
    c: Coincident(g4,g0)
    c: Distance(g0,g1) = 600.075
    c: Distance(g0,g3) = 787.4
    c: Distance(g3,g2) = 295.275
    c: Diameter(g5) = 6.35
    c: Distance(g5,g0) = 31.75
    c: Distance(g5,g4) = 46.0502
    c: Vertical(g2)
    c: Distance(g2,g3) = 177.8
    c: Coincident(g6,g2)
    c: Horizontal(g6)
    c: Coincident(g7,g6)
    c: Vertical(g7)
    c: Coincident(g8,g7)
    c: Horizontal(g8)
    c: Distance(g7,g6) = 7.9502
    c: Distance(g6,g2) = 9.525
    c: Coincident(g8,g1)
    c: Diameter(g9) = 6.35
    c: Coincident(g5,g10)
    c: Coincident(g9,g10)
    c: Angle(g10) = 0
    c: Diameter(g11) = 6.35
    c: Coincident(g9,g12)
    c: Coincident(g11,g12)
    c: Equal(g10,g12)
    c: Parallel(g12,g10)
    c: Diameter(g13) = 6.35
    c: Coincident(g11,g14)
    c: Coincident(g13,g14)
    c: Equal(g10,g14)
    c: Parallel(g14,g10)
    c: Diameter(g15) = 6.35
    c: Coincident(g13,g16)
    c: Coincident(g15,g16)
    c: Equal(g10,g16)
    c: Parallel(g16,g10)
    c: Diameter(g17) = 6.35
    c: Coincident(g15,g18)
    c: Coincident(g17,g18)
    c: Equal(g10,g18)
    c: Parallel(g18,g10)
    c: Diameter(g19) = 6.35
    c: Coincident(g17,g20)
    c: Coincident(g19,g20)
    c: Equal(g10,g20)
    c: Parallel(g20,g10)
    c: Diameter(g21) = 6.35
    c: Coincident(g19,g22)
    c: Coincident(g21,g22)
    c: Equal(g10,g22)
    c: Parallel(g22,g10)
    c: Diameter(g23) = 6.35
    c: Coincident(g21,g24)
    c: Coincident(g23,g24)
    c: Equal(g10,g24)
    c: Parallel(g24,g10)
    c: Diameter(g25) = 6.35
    c: Coincident(g23,g26)
    c: Coincident(g25,g26)
    c: Equal(g10,g26)
    c: Parallel(g26,g10)
    c: Diameter(g27) = 6.35
    c: Coincident(g25,g28)
    c: Coincident(g27,g28)
    c: Equal(g10,g28)
    c: Parallel(g28,g10)
    c: Diameter(g29) = 6.35
    c: Coincident(g5,g30)
    c: Coincident(g29,g30)
    c: Equal(g30,g10)
    c: Perpendicular(g30,g10)
    c: Diameter(g31) = 6.35
    c: Coincident(g29,g32)
    c: Coincident(g31,g32)
    c: Equal(g10,g32)
    c: Parallel(g32,g10)
    c: Diameter(g33) = 6.35
    c: Coincident(g31,g34)
    c: Coincident(g33,g34)
    c: Equal(g10,g34)
    c: Parallel(g34,g10)
    c: Diameter(g35) = 6.35
    c: Coincident(g33,g36)
    c: Coincident(g35,g36)
    c: Equal(g10,g36)
    c: Parallel(g36,g10)
    c: Diameter(g37) = 6.35
    c: Coincident(g35,g38)
    c: Coincident(g37,g38)
    c: Equal(g10,g38)
    c: Parallel(g38,g10)
    c: Diameter(g39) = 6.35
    c: Coincident(g37,g40)
    c: Coincident(g39,g40)
    c: Equal(g10,g40)
    c: Parallel(g40,g10)
    c: Diameter(g41) = 6.35
    c: Coincident(g39,g42)
    c: Coincident(g41,g42)
    c: Equal(g10,g42)
    c: Parallel(g42,g10)
    c: Diameter(g43) = 6.35
    c: Coincident(g41,g44)
    c: Coincident(g43,g44)
    c: Equal(g10,g44)
    c: Parallel(g44,g10)
    c: Diameter(g45) = 6.35
    c: Coincident(g43,g46)
    c: Coincident(g45,g46)
    c: Equal(g10,g46)
    c: Parallel(g46,g10)
    c: Diameter(g47) = 6.35
    c: Coincident(g45,g48)
    c: Coincident(g47,g48)
    c: Equal(g10,g48)
    c: Parallel(g48,g10)
    c: Diameter(g49) = 6.35
    c: Coincident(g47,g50)
    c: Coincident(g49,g50)
    c: Equal(g10,g50)
    c: Parallel(g50,g10)
    c: Diameter(g51) = 6.35
    c: Coincident(g29,g52)
    c: Coincident(g51,g52)
    c: Equal(g30,g52)
    c: Perpendicular(g52,g10)
    c: Diameter(g53) = 6.35
    c: Coincident(g51,g54)
    c: Coincident(g53,g54)
    c: Equal(g10,g54)
    c: Parallel(g54,g10)
    c: Diameter(g55) = 6.35
    c: Coincident(g53,g56)
    c: Coincident(g55,g56)
    c: Equal(g10,g56)
    c: Parallel(g56,g10)
    c: Diameter(g57) = 6.35
    c: Coincident(g55,g58)
    c: Coincident(g57,g58)
    c: Equal(g10,g58)
    c: Parallel(g58,g10)
    c: Diameter(g59) = 6.35
    c: Coincident(g57,g60)
    c: Coincident(g59,g60)
    c: Equal(g10,g60)
    c: Parallel(g60,g10)
    c: Diameter(g61) = 6.35
    c: Coincident(g59,g62)
    c: Coincident(g61,g62)
    c: Equal(g10,g62)
    c: Parallel(g62,g10)
    c: Diameter(g63) = 6.35
    c: Coincident(g61,g64)
    c: Coincident(g63,g64)
    c: Equal(g10,g64)
    c: Parallel(g64,g10)
    c: Diameter(g65) = 6.35
    c: Coincident(g63,g66)
    c: Coincident(g65,g66)
    c: Equal(g10,g66)
    c: Parallel(g66,g10)
    c: Diameter(g67) = 6.35
    c: Coincident(g65,g68)
    c: Coincident(g67,g68)
    c: Equal(g10,g68)
    c: Parallel(g68,g10)
    c: Diameter(g69) = 6.35
    c: Coincident(g67,g70)
    c: Coincident(g69,g70)
    c: Equal(g10,g70)
    c: Parallel(g70,g10)
    c: Diameter(g71) = 6.35
    c: Coincident(g69,g72)
    c: Coincident(g71,g72)
    c: Equal(g10,g72)
    c: Parallel(g72,g10)
    c: Diameter(g73) = 6.35
    c: Coincident(g51,g74)
    c: Coincident(g73,g74)
    c: Equal(g30,g74)
    c: Perpendicular(g74,g10)
    c: Diameter(g75) = 6.35
    c: Coincident(g73,g76)
    c: Coincident(g75,g76)
    c: Equal(g10,g76)
    c: Parallel(g76,g10)
    c: Diameter(g77) = 6.35
    c: Coincident(g75,g78)
    c: Coincident(g77,g78)
    c: Equal(g10,g78)
    c: Parallel(g78,g10)
    c: Diameter(g79) = 6.35
    c: Coincident(g77,g80)
    c: Coincident(g79,g80)
    c: Equal(g10,g80)
    c: Parallel(g80,g10)
    c: Diameter(g81) = 6.35
    c: Coincident(g79,g82)
    c: Coincident(g81,g82)
    c: Equal(g10,g82)
    c: Parallel(g82,g10)
    c: Diameter(g83) = 6.35
    c: Coincident(g81,g84)
    c: Coincident(g83,g84)
    c: Equal(g10,g84)
    c: Parallel(g84,g10)
    c: Diameter(g85) = 6.35
    c: Coincident(g83,g86)
    c: Coincident(g85,g86)
    c: Equal(g10,g86)
    c: Parallel(g86,g10)
    c: Diameter(g87) = 6.35
    c: Coincident(g85,g88)
    c: Coincident(g87,g88)
    c: Equal(g10,g88)
    c: Parallel(g88,g10)
    c: Diameter(g89) = 6.35
    c: Coincident(g87,g90)
    c: Coincident(g89,g90)
    c: Equal(g10,g90)
    c: Parallel(g90,g10)
    c: Diameter(g91) = 6.35
    c: Coincident(g89,g92)
    c: Coincident(g91,g92)
    c: Equal(g10,g92)
    c: Parallel(g92,g10)
    c: Diameter(g93) = 6.35
    c: Coincident(g91,g94)
    c: Coincident(g93,g94)
    c: Equal(g10,g94)
    c: Parallel(g94,g10)
    c: Diameter(g95) = 6.35
    c: Coincident(g73,g96)
    c: Coincident(g95,g96)
    c: Equal(g30,g96)
    c: Perpendicular(g96,g10)
    c: Diameter(g97) = 6.35
    c: Coincident(g95,g98)
    c: Coincident(g97,g98)
    c: Equal(g10,g98)
    c: Parallel(g98,g10)
    c: Diameter(g99) = 6.35
    c: Coincident(g97,g100)
    c: Coincident(g99,g100)
    c: Equal(g10,g100)
    c: Parallel(g100,g10)
    c: Diameter(g101) = 6.35
    c: Coincident(g99,g102)
    c: Coincident(g101,g102)
    c: Equal(g10,g102)
    c: Parallel(g102,g10)
    c: Diameter(g103) = 6.35
    c: Coincident(g101,g104)
    c: Coincident(g103,g104)
    c: Equal(g10,g104)
    c: Parallel(g104,g10)
    c: Diameter(g105) = 6.35
    c: Coincident(g103,g106)
    c: Coincident(g105,g106)
    c: Equal(g10,g106)
    c: Parallel(g106,g10)
    c: Diameter(g107) = 6.35
    c: Coincident(g105,g108)
    c: Coincident(g107,g108)
    c: Equal(g10,g108)
    c: Parallel(g108,g10)
    c: Diameter(g109) = 6.35
    c: Coincident(g107,g110)
    c: Coincident(g109,g110)
    c: Equal(g10,g110)
    c: Parallel(g110,g10)
    c: Diameter(g111) = 6.35
    c: Coincident(g109,g112)
    c: Coincident(g111,g112)
    c: Equal(g10,g112)
    c: Parallel(g112,g10)
    c: Diameter(g113) = 6.35
    c: Coincident(g111,g114)
    c: Coincident(g113,g114)
    c: Equal(g10,g114)
    c: Parallel(g114,g10)
    c: Diameter(g115) = 6.35
    c: Coincident(g113,g116)
    c: Coincident(g115,g116)
    c: Equal(g10,g116)
    c: Parallel(g116,g10)
    c: Diameter(g117) = 6.35
    c: Coincident(g95,g118)
    c: Coincident(g117,g118)
    c: Equal(g30,g118)
    c: Perpendicular(g118,g10)
    c: Diameter(g119) = 6.35
    c: Coincident(g117,g120)
    c: Coincident(g119,g120)
    c: Equal(g10,g120)
    c: Parallel(g120,g10)
    c: Diameter(g121) = 6.35
    c: Coincident(g119,g122)
    c: Coincident(g121,g122)
    c: Equal(g10,g122)
    c: Parallel(g122,g10)
    c: Diameter(g123) = 6.35
    c: Coincident(g121,g124)
    c: Coincident(g123,g124)
    c: Equal(g10,g124)
    c: Parallel(g124,g10)
    c: Diameter(g125) = 6.35
    c: Coincident(g123,g126)
    c: Coincident(g125,g126)
    c: Equal(g10,g126)
    c: Parallel(g126,g10)
    c: Diameter(g127) = 6.35
    c: Coincident(g125,g128)
    c: Coincident(g127,g128)
    c: Equal(g10,g128)
    c: Parallel(g128,g10)
    c: Diameter(g129) = 6.35
    c: Coincident(g127,g130)
    c: Coincident(g129,g130)
    c: Equal(g10,g130)
    c: Parallel(g130,g10)
    c: Diameter(g131) = 6.35
    c: Coincident(g129,g132)
    c: Coincident(g131,g132)
    c: Equal(g10,g132)
    c: Parallel(g132,g10)
    c: Diameter(g133) = 6.35
    c: Coincident(g131,g134)
    c: Coincident(g133,g134)
    c: Equal(g10,g134)
    c: Parallel(g134,g10)
    c: Diameter(g135) = 6.35
    c: Coincident(g133,g136)
    c: Coincident(g135,g136)
    c: Equal(g10,g136)
    c: Parallel(g136,g10)
    c: Diameter(g137) = 6.35
    c: Coincident(g135,g138)
    c: Coincident(g137,g138)
    c: Equal(g10,g138)
    c: Parallel(g138,g10)
    c: Diameter(g139) = 6.35
    c: Coincident(g117,g140)
    c: Coincident(g139,g140)
    c: Equal(g30,g140)
    c: Perpendicular(g140,g10)
    c: Diameter(g141) = 6.35
    c: Coincident(g139,g142)
    c: Coincident(g141,g142)
    c: Equal(g10,g142)
    c: Parallel(g142,g10)
    c: Diameter(g143) = 6.35
    c: Coincident(g141,g144)
    c: Coincident(g143,g144)
    c: Equal(g10,g144)
    c: Parallel(g144,g10)
    c: Diameter(g145) = 6.35
    c: Coincident(g143,g146)
    c: Coincident(g145,g146)
    c: Equal(g10,g146)
    c: Parallel(g146,g10)
    c: Diameter(g147) = 6.35
    c: Coincident(g145,g148)
    c: Coincident(g147,g148)
    c: Equal(g10,g148)
    c: Parallel(g148,g10)
    c: Diameter(g149) = 6.35
    c: Coincident(g147,g150)
    c: Coincident(g149,g150)
    c: Equal(g10,g150)
    c: Parallel(g150,g10)
    c: Diameter(g151) = 6.35
    c: Coincident(g149,g152)
    c: Coincident(g151,g152)
    c: Equal(g10,g152)
    c: Parallel(g152,g10)
    c: Diameter(g153) = 6.35
    c: Coincident(g151,g154)
    c: Coincident(g153,g154)
    c: Equal(g10,g154)
    c: Parallel(g154,g10)
    c: Diameter(g155) = 6.35
    c: Coincident(g153,g156)
    c: Coincident(g155,g156)
    c: Equal(g10,g156)
    c: Parallel(g156,g10)
    c: Diameter(g157) = 6.35
    c: Coincident(g155,g158)
    c: Coincident(g157,g158)
    c: Equal(g10,g158)
    c: Parallel(g158,g10)
    c: Diameter(g159) = 6.35
    c: Coincident(g157,g160)
    c: Coincident(g159,g160)
    c: Equal(g10,g160)
    c: Parallel(g160,g10)
    c: Diameter(g161) = 6.35
    c: Coincident(g139,g162)
    c: Coincident(g161,g162)
    c: Equal(g30,g162)
    c: Perpendicular(g162,g10)
    c: Diameter(g163) = 6.35
    c: Coincident(g161,g164)
    c: Coincident(g163,g164)
    c: Equal(g10,g164)
    c: Parallel(g164,g10)
    c: Diameter(g165) = 6.35
    c: Coincident(g163,g166)
    c: Coincident(g165,g166)
    c: Equal(g10,g166)
    c: Parallel(g166,g10)
    c: Diameter(g167) = 6.35
    c: Coincident(g165,g168)
    c: Coincident(g167,g168)
    c: Equal(g10,g168)
    c: Parallel(g168,g10)
    c: Diameter(g169) = 6.35
    c: Coincident(g167,g170)
    c: Coincident(g169,g170)
    c: Equal(g10,g170)
    c: Parallel(g170,g10)
    c: Diameter(g171) = 6.35
    c: Coincident(g169,g172)
    c: Coincident(g171,g172)
    c: Equal(g10,g172)
    c: Parallel(g172,g10)
    c: Diameter(g173) = 6.35
    c: Coincident(g171,g174)
    c: Coincident(g173,g174)
    c: Equal(g10,g174)
    c: Parallel(g174,g10)
    c: Diameter(g175) = 6.35
    c: Coincident(g173,g176)
    c: Coincident(g175,g176)
    c: Equal(g10,g176)
    c: Parallel(g176,g10)
    c: Diameter(g177) = 6.35
    c: Coincident(g175,g178)
    c: Coincident(g177,g178)
    c: Equal(g10,g178)
    c: Parallel(g178,g10)
    c: Diameter(g179) = 6.35
    c: Coincident(g177,g180)
    c: Coincident(g179,g180)
    c: Equal(g10,g180)
    c: Parallel(g180,g10)
    c: Diameter(g181) = 6.35
    c: Coincident(g179,g182)
    c: Coincident(g181,g182)
    c: Equal(g10,g182)
    c: Parallel(g182,g10)
    c: Diameter(g183) = 6.35
    c: Coincident(g161,g184)
    c: Coincident(g183,g184)
    c: Equal(g30,g184)
    c: Perpendicular(g184,g10)
    c: Diameter(g185) = 6.35
    c: Coincident(g183,g186)
    c: Coincident(g185,g186)
    c: Equal(g10,g186)
    c: Parallel(g186,g10)
    c: Diameter(g187) = 6.35
    c: Coincident(g185,g188)
    c: Coincident(g187,g188)
    c: Equal(g10,g188)
    c: Parallel(g188,g10)
    c: Diameter(g189) = 6.35
    c: Coincident(g187,g190)
    c: Coincident(g189,g190)
    c: Equal(g10,g190)
    c: Parallel(g190,g10)
    c: Diameter(g191) = 6.35
    c: Coincident(g189,g192)
    c: Coincident(g191,g192)
    c: Equal(g10,g192)
    c: Parallel(g192,g10)
    c: Diameter(g193) = 6.35
    c: Coincident(g191,g194)
    c: Coincident(g193,g194)
    c: Equal(g10,g194)
    c: Parallel(g194,g10)
    c: Diameter(g195) = 6.35
    c: Coincident(g193,g196)
    c: Coincident(g195,g196)
    c: Equal(g10,g196)
    c: Parallel(g196,g10)
    c: Diameter(g197) = 6.35
    c: Coincident(g195,g198)
    c: Coincident(g197,g198)
    c: Equal(g10,g198)
    c: Parallel(g198,g10)
    c: Diameter(g199) = 6.35
    c: Coincident(g197,g200)
    c: Coincident(g199,g200)
    c: Equal(g10,g200)
    c: Parallel(g200,g10)
    c: Diameter(g201) = 6.35
    c: Coincident(g199,g202)
    c: Coincident(g201,g202)
    c: Equal(g10,g202)
    c: Parallel(g202,g10)
    c: Diameter(g203) = 6.35
    c: Coincident(g201,g204)
    c: Coincident(g203,g204)
    c: Equal(g10,g204)
    c: Parallel(g204,g10)
    c: Diameter(g205) = 6.35
    c: Coincident(g183,g206)
    c: Coincident(g205,g206)
    c: Equal(g30,g206)
    c: Perpendicular(g206,g10)
    c: Diameter(g207) = 6.35
    c: Coincident(g205,g208)
    c: Coincident(g207,g208)
    c: Equal(g10,g208)
    c: Parallel(g208,g10)
    c: Diameter(g209) = 6.35
    c: Coincident(g207,g210)
    c: Coincident(g209,g210)
    c: Equal(g10,g210)
    c: Parallel(g210,g10)
    c: Diameter(g211) = 6.35
    c: Coincident(g209,g212)
    c: Coincident(g211,g212)
    c: Equal(g10,g212)
    c: Parallel(g212,g10)
    c: Diameter(g213) = 6.35
    c: Coincident(g211,g214)
    c: Coincident(g213,g214)
    c: Equal(g10,g214)
    c: Parallel(g214,g10)
    c: Diameter(g215) = 6.35
    c: Coincident(g213,g216)
    c: Coincident(g215,g216)
    c: Equal(g10,g216)
    c: Parallel(g216,g10)
    c: Diameter(g217) = 6.35
    c: Coincident(g215,g218)
    c: Coincident(g217,g218)
    c: Equal(g10,g218)
    c: Parallel(g218,g10)
    c: Diameter(g219) = 6.35
    c: Coincident(g217,g220)
    c: Coincident(g219,g220)
    c: Equal(g10,g220)
    c: Parallel(g220,g10)
    c: Diameter(g221) = 6.35
    c: Coincident(g219,g222)
    c: Coincident(g221,g222)
    c: Equal(g10,g222)
    c: Parallel(g222,g10)
    c: Diameter(g223) = 6.35
    c: Coincident(g221,g224)
    c: Coincident(g223,g224)
    c: Equal(g10,g224)
    c: Parallel(g224,g10)
    c: Diameter(g225) = 6.35
    c: Coincident(g223,g226)
    c: Coincident(g225,g226)
    c: Equal(g10,g226)
    c: Parallel(g226,g10)
    c: Diameter(g227) = 6.35
    c: Coincident(g205,g228)
    c: Coincident(g227,g228)
    c: Equal(g30,g228)
    c: Perpendicular(g228,g10)
    c: Diameter(g229) = 6.35
    c: Coincident(g227,g230)
    c: Coincident(g229,g230)
    c: Equal(g10,g230)
    c: Parallel(g230,g10)
    c: Diameter(g231) = 6.35
    c: Coincident(g229,g232)
    c: Coincident(g231,g232)
    c: Equal(g10,g232)
    c: Parallel(g232,g10)
    c: Diameter(g233) = 6.35
    c: Coincident(g231,g234)
    c: Coincident(g233,g234)
    c: Equal(g10,g234)
    c: Parallel(g234,g10)
    c: Diameter(g235) = 6.35
    c: Coincident(g233,g236)
    c: Coincident(g235,g236)
    c: Equal(g10,g236)
    c: Parallel(g236,g10)
    c: Diameter(g237) = 6.35
    c: Coincident(g235,g238)
    c: Coincident(g237,g238)
    c: Equal(g10,g238)
    c: Parallel(g238,g10)
    c: Diameter(g239) = 6.35
    c: Coincident(g237,g240)
    c: Coincident(g239,g240)
    c: Equal(g10,g240)
    c: Parallel(g240,g10)
    c: Diameter(g241) = 6.35
    c: Coincident(g239,g242)
    c: Coincident(g241,g242)
    c: Equal(g10,g242)
    c: Parallel(g242,g10)
    c: Diameter(g243) = 6.35
    c: Coincident(g241,g244)
    c: Coincident(g243,g244)
    c: Equal(g10,g244)
    c: Parallel(g244,g10)
    c: Diameter(g245) = 6.35
    c: Coincident(g243,g246)
    c: Coincident(g245,g246)
    c: Equal(g10,g246)
    c: Parallel(g246,g10)
    c: Diameter(g247) = 6.35
    c: Coincident(g245,g248)
    c: Coincident(g247,g248)
    c: Equal(g10,g248)
    c: Parallel(g248,g10)
    c: Diameter(g249) = 6.35
    c: Coincident(g227,g250)
    c: Coincident(g249,g250)
    c: Equal(g30,g250)
    c: Perpendicular(g250,g10)
    c: Diameter(g251) = 6.35
    c: Coincident(g249,g252)
    c: Coincident(g251,g252)
    c: Equal(g10,g252)
    c: Parallel(g252,g10)
    c: Diameter(g253) = 6.35
    c: Coincident(g251,g254)
    c: Coincident(g253,g254)
    c: Equal(g10,g254)
    c: Parallel(g254,g10)
    c: Diameter(g255) = 6.35
    c: Coincident(g253,g256)
    c: Coincident(g255,g256)
    c: Equal(g10,g256)
    c: Parallel(g256,g10)
    c: Diameter(g257) = 6.35
    c: Coincident(g255,g258)
    c: Coincident(g257,g258)
    c: Equal(g10,g258)
    c: Parallel(g258,g10)
    c: Diameter(g259) = 6.35
    c: Coincident(g257,g260)
    c: Coincident(g259,g260)
    c: Equal(g10,g260)
    c: Parallel(g260,g10)
    c: Diameter(g261) = 6.35
    c: Coincident(g259,g262)
    c: Coincident(g261,g262)
    c: Equal(g10,g262)
    c: Parallel(g262,g10)
    c: Diameter(g263) = 6.35
    c: Coincident(g261,g264)
    c: Coincident(g263,g264)
    c: Equal(g10,g264)
    c: Parallel(g264,g10)
    c: Diameter(g265) = 6.35
    c: Coincident(g263,g266)
    c: Coincident(g265,g266)
    c: Equal(g10,g266)
    c: Parallel(g266,g10)
    c: Diameter(g267) = 6.35
    c: Coincident(g265,g268)
    c: Coincident(g267,g268)
    c: Equal(g10,g268)
    c: Parallel(g268,g10)
    c: Diameter(g269) = 6.35
    c: Coincident(g267,g270)
    c: Coincident(g269,g270)
    c: Equal(g10,g270)
    c: Parallel(g270,g10)
    c: Diameter(g271) = 6.35
    c: Coincident(g249,g272)
    c: Coincident(g271,g272)
    c: Equal(g30,g272)
    c: Perpendicular(g272,g10)
    c: Diameter(g273) = 6.35
    c: Coincident(g271,g274)
    c: Coincident(g273,g274)
    c: Equal(g10,g274)
    c: Parallel(g274,g10)
    c: Diameter(g275) = 6.35
    c: Coincident(g273,g276)
    c: Coincident(g275,g276)
    c: Equal(g10,g276)
    c: Parallel(g276,g10)
    c: Diameter(g277) = 6.35
    c: Coincident(g275,g278)
    c: Coincident(g277,g278)
    c: Equal(g10,g278)
    c: Parallel(g278,g10)
    c: Diameter(g279) = 6.35
    c: Coincident(g277,g280)
    c: Coincident(g279,g280)
    c: Equal(g10,g280)
    c: Parallel(g280,g10)
    c: Diameter(g281) = 6.35
    c: Coincident(g271,g282)
    c: Coincident(g281,g282)
    c: Equal(g30,g282)
    c: Perpendicular(g282,g10)
    c: Diameter(g283) = 6.35
    c: Coincident(g281,g284)
    c: Coincident(g283,g284)
    c: Equal(g10,g284)
    c: Parallel(g284,g10)
    c: Diameter(g285) = 6.35
    c: Coincident(g283,g286)
    c: Coincident(g285,g286)
    c: Equal(g10,g286)
    c: Parallel(g286,g10)
    c: Diameter(g287) = 6.35
    c: Coincident(g285,g288)
    c: Coincident(g287,g288)
    c: Equal(g10,g288)
    c: Parallel(g288,g10)
    c: Diameter(g289) = 6.35
    c: Coincident(g287,g290)
    c: Coincident(g289,g290)
    c: Equal(g10,g290)
    c: Parallel(g290,g10)
    c: Diameter(g291) = 6.35
    c: Coincident(g281,g292)
    c: Coincident(g291,g292)
    c: Equal(g30,g292)
    c: Perpendicular(g292,g10)
    c: Diameter(g293) = 6.35
    c: Coincident(g291,g294)
    c: Coincident(g293,g294)
    c: Equal(g10,g294)
    c: Parallel(g294,g10)
    c: Diameter(g295) = 6.35
    c: Coincident(g293,g296)
    c: Coincident(g295,g296)
    c: Equal(g10,g296)
    c: Parallel(g296,g10)
    c: Diameter(g297) = 6.35
    c: Coincident(g295,g298)
    c: Coincident(g297,g298)
    c: Equal(g10,g298)
    c: Parallel(g298,g10)
    c: Diameter(g299) = 6.35
    c: Coincident(g297,g300)
    c: Coincident(g299,g300)
    c: Equal(g10,g300)
    c: Parallel(g300,g10)
FEATURE [Part::Extrusion] Extrude
  Base = -> Sketch
  Dir = (0,0,1)
  DirMode = 2
  FaceMakerClass = Part::FaceMakerBullseye
  LengthFwd = 5.9944
  LengthRev = 0
  Solid = true
  Symmetric = false
FEATURE [TechDraw::DrawSVGTemplate] Template
  Height = 215.9
  Orientation = 1
  Width = 279.4
FEATURE [TechDraw::DrawProjGroupItem] ProjItem  label="Front"
  CoarseView = false
  Direction = (0,0,1)
  Focus = 100
  HardHidden = false
  IsoCount = 0
  IsoHidden = false
  IsoVisible = false
  LockPosition = true
  Perspective = false
  Rotation = 0
  RotationVector = (-1,0,0)
  Scale = 0.2
  ScaleType = 2
  SeamHidden = false
  SeamVisible = true
  SmoothHidden = false
  SmoothVisible = true
  Source = -> [Extrude]
  Type = 0
  X = 0
  XDirection = (1,-1e-16,0)
  Y = 0
FEATURE [TechDraw::DrawProjGroupItem] ProjItem001  label="Left"
  CoarseView = false
  Direction = (-1,1e-16,1e-16)
  Focus = 100
  HardHidden = false
  IsoCount = 0
  IsoHidden = false
  IsoVisible = false
  LockPosition = false
  Perspective = false
  Rotation = 0
  RotationVector = (1,0,0)
  Scale = 0.2
  ScaleType = 2
  SeamHidden = false
  SeamVisible = true
  SmoothHidden = false
  SmoothVisible = true
  Source = -> [Extrude]
  Type = 1
  X = 80.6565
  XDirection = (1e-16,0,1)
  Y = 0
FEATURE [TechDraw::DrawProjGroup] ProjGroup
  Anchor = -> ProjItem
  AutoDistribute = true
  LockPosition = false
  ProjectionType = 0
  Rotation = 0
  Scale = 0.2
  ScaleType = 2
  Source = -> [Extrude]
  Views = -> [ProjItem,ProjItem001]
  X = 150.88
  Y = 93.9359
  spacingX = 15.0114
  spacingY = 15.0114
FEATURE [TechDraw::DrawHatch] Hatch  label="HatchF0"
  HatchPattern = <path>
  Source = -> ProjItem [Face0]
FEATURE [TechDraw::DrawHatch] Hatch001  label="Hatch001F0"
  HatchPattern = <path>
  Source = -> ProjItem001 [Face0]
FEATURE [TechDraw::DrawViewDimension] Dimension
  Arbitrary = false
  ArbitraryTolerances = false
  EqualTolerance = true
  FormatSpec = %.3f
  FormatSpecOverTolerance = %+.3f
  FormatSpecUnderTolerance = %+.3f
  Inverted = false
  LockPosition = false
  MeasureType = 1
  OverTolerance = 0
  References2D = -> [ProjItem]
  Rotation = 0
  ScaleType = 0
  TheoreticalExact = false
  Type = 1
  UnderTolerance = 0
  X = 3.50259
  Y = 104.504
FEATURE [TechDraw::DrawViewDimension] Dimension001
  Arbitrary = false
  ArbitraryTolerances = false
  EqualTolerance = true
  FormatSpec = %.3f
  FormatSpecOverTolerance = %+.3f
  FormatSpecUnderTolerance = %+.3f
  Inverted = false
  LockPosition = false
  MeasureType = 1
  OverTolerance = 0
  References2D = -> [ProjItem001]
  Rotation = 0
  ScaleType = 0
  TheoreticalExact = false
  Type = 1
  UnderTolerance = 0
  X = 19.1934
  Y = 68.1151
FEATURE [TechDraw::DrawViewDimension] Dimension002
  Arbitrary = false
  ArbitraryTolerances = false
  EqualTolerance = true
  FormatSpec = %.3f
  FormatSpecOverTolerance = %+.3f
  FormatSpecUnderTolerance = %+.3f
  Inverted = false
  LockPosition = false
  MeasureType = 1
  OverTolerance = 0
  References2D = -> [ProjItem]
  Rotation = 0
  ScaleType = 0
  TheoreticalExact = false
  Type = 2
  UnderTolerance = 0
  X = -89.4819
  Y = 0.810546
FEATURE [TechDraw::DrawViewDimension] Dimension003
  Arbitrary = false
  ArbitraryTolerances = false
  EqualTolerance = true
  FormatSpec = ⌀%.3f
  FormatSpecOverTolerance = %+.3f
  FormatSpecUnderTolerance = %+.3f
  Inverted = false
  LockPosition = false
  MeasureType = 1
  OverTolerance = 0
  References2D = -> [ProjItem]
  Rotation = 0
  ScaleType = 0
  TheoreticalExact = false
  Type = 5
  UnderTolerance = 0
  X = -69.1699
  Y = 92.9925
FEATURE [TechDraw::DrawViewDimension] Dimension004
  Arbitrary = false
  ArbitraryTolerances = false
  EqualTolerance = true
  FormatSpec = %.3f
  FormatSpecOverTolerance = %+.3f
  FormatSpecUnderTolerance = %+.3f
  Inverted = false
  LockPosition = false
  MeasureType = 1
  OverTolerance = 0
  References2D = -> [ProjItem]
  Rotation = 0
  ScaleType = 0
  TheoreticalExact = false
  Type = 2
  UnderTolerance = 0
  X = -39.3212
  Y = 93.3367
FEATURE [TechDraw::DrawViewDimension] Dimension005
  Arbitrary = false
  ArbitraryTolerances = false
  EqualTolerance = true
  FormatSpec = %.3f
  FormatSpecOverTolerance = %+.3f
  FormatSpecUnderTolerance = %+.3f
  Inverted = false
  LockPosition = false
  MeasureType = 1
  OverTolerance = 0
  References2D = -> [ProjItem]
  Rotation = 0
  ScaleType = 0
  TheoreticalExact = false
  Type = 1
  UnderTolerance = 0
  X = -75.0723
  Y = 62.6699
FEATURE [TechDraw::DrawViewDimension] Dimension006
  Arbitrary = false
  ArbitraryTolerances = false
  EqualTolerance = true
  FormatSpec = %.3f
  FormatSpecOverTolerance = %+.3f
  FormatSpecUnderTolerance = %+.3f
  Inverted = false
  LockPosition = false
  MeasureType = 1
  OverTolerance = 0
  References2D = -> [ProjItem]
  Rotation = 0
  ScaleType = 0
  TheoreticalExact = false
  Type = 2
  UnderTolerance = 0
  X = -28.0142
  Y = 93.0347
FEATURE [TechDraw::DrawViewDimension] Dimension007
  Arbitrary = false
  ArbitraryTolerances = false
  EqualTolerance = true
  FormatSpec = %.3f
  FormatSpecOverTolerance = %+.3f
  FormatSpecUnderTolerance = %+.3f
  Inverted = false
  LockPosition = false
  MeasureType = 1
  OverTolerance = 0
  References2D = -> [ProjItem]
  Rotation = 0
  ScaleType = 0
  TheoreticalExact = false
  Type = 1
  UnderTolerance = 0
  X = -75.1463
  Y = 50.6688
FEATURE [TechDraw::DrawViewDimension] Dimension008
  Arbitrary = false
  ArbitraryTolerances = false
  EqualTolerance = true
  FormatSpec = %.3f
  FormatSpecOverTolerance = %+.3f
  FormatSpecUnderTolerance = %+.3f
  Inverted = false
  LockPosition = false
  MeasureType = 1
  OverTolerance = 0
  References2D = -> [ProjItem]
  Rotation = 0
  ScaleType = 0
  TheoreticalExact = false
  Type = 1
  UnderTolerance = 0
  X = -28.1257
  Y = -19.5461
FEATURE [TechDraw::DrawViewDimension] Dimension009
  Arbitrary = false
  ArbitraryTolerances = false
  EqualTolerance = true
  FormatSpec = %.3f
  FormatSpecOverTolerance = %+.3f
  FormatSpecUnderTolerance = %+.3f
  Inverted = false
  LockPosition = false
  MeasureType = 1
  OverTolerance = 0
  References2D = -> [ProjItem]
  Rotation = 0
  ScaleType = 0
  TheoreticalExact = false
  Type = 1
  UnderTolerance = 0
  X = 29.8638
  Y = -19.4889
FEATURE [TechDraw::DrawViewDimension] Dimension010
  Arbitrary = false
  ArbitraryTolerances = false
  EqualTolerance = true
  FormatSpec = %.3f
  FormatSpecOverTolerance = %+.3f
  FormatSpecUnderTolerance = %+.3f
  Inverted = false
  LockPosition = false
  MeasureType = 1
  OverTolerance = 0
  References2D = -> [ProjItem]
  Rotation = 0
  ScaleType = 0
  TheoreticalExact = false
  Type = 1
  UnderTolerance = 0
  X = -20.877
  Y = -51.0274
FEATURE [TechDraw::DrawViewDimension] Dimension011
  Arbitrary = false
  ArbitraryTolerances = false
  EqualTolerance = true
  FormatSpec = %.3f
  FormatSpecOverTolerance = %+.3f
  FormatSpecUnderTolerance = %+.3f
  Inverted = false
  LockPosition = false
  MeasureType = 1
  OverTolerance = 0
  References2D = -> [ProjItem]
  Rotation = 0
  ScaleType = 0
  TheoreticalExact = false
  Type = 2
  UnderTolerance = 0
  X = 4.65409
  Y = -29.3167
FEATURE [TechDraw::DrawViewDimension] Dimension012
  Arbitrary = false
  ArbitraryTolerances = false
  EqualTolerance = true
  FormatSpec = %.3f
  FormatSpecOverTolerance = %+.3f
  FormatSpecUnderTolerance = %+.3f
  Inverted = false
  LockPosition = false
  MeasureType = 1
  OverTolerance = 0
  References2D = -> [ProjItem]
  Rotation = 0
  ScaleType = 0
  TheoreticalExact = false
  Type = 2
  UnderTolerance = 0
  X = 26.2757
  Y = -61.755
FEATURE [TechDraw::DrawViewAnnotation] Annotation
  Font = osifont
  LineSpace = 80
  LockPosition = false
  MaxWidth = -1
  Rotation = 0
  ScaleType = 0
  Text = Figure S2 (Inverted 2) | Panel 9 [left side interior baffle] | Quantity: 1
  TextSize = 5.0038
  TextStyle = 0
  X = 45.5266
  Y = 195.58
FEATURE [TechDraw::DrawViewAnnotation] Annotation002
  Font = osifont
  LineSpace = 80
  LockPosition = false
  MaxWidth = -1
  Rotation = 0
  ScaleType = 0
  Text = Units: Inches
  TextSize = 5.0038
  TextStyle = 0
  X = 259.08
  Y = 5.08
FEATURE [TechDraw::DrawPage] Page
  KeepUpdated = true
  NextBalloonIndex = 1
  ProjectionType = 0
  Template = -> Template
  Views = -> [ProjGroup,Dimension,Dimension001,Dimension002,Dimension003,Dimension004,Dimension005,Dimension006,Dimension007,Dimension008,Dimension009,Dimension010,Dimension011,Dimension012,Annotation,Annotation002]
note: 2 file-system paths scrubbed to <path> (originals preserved in the JSON sidecar)
